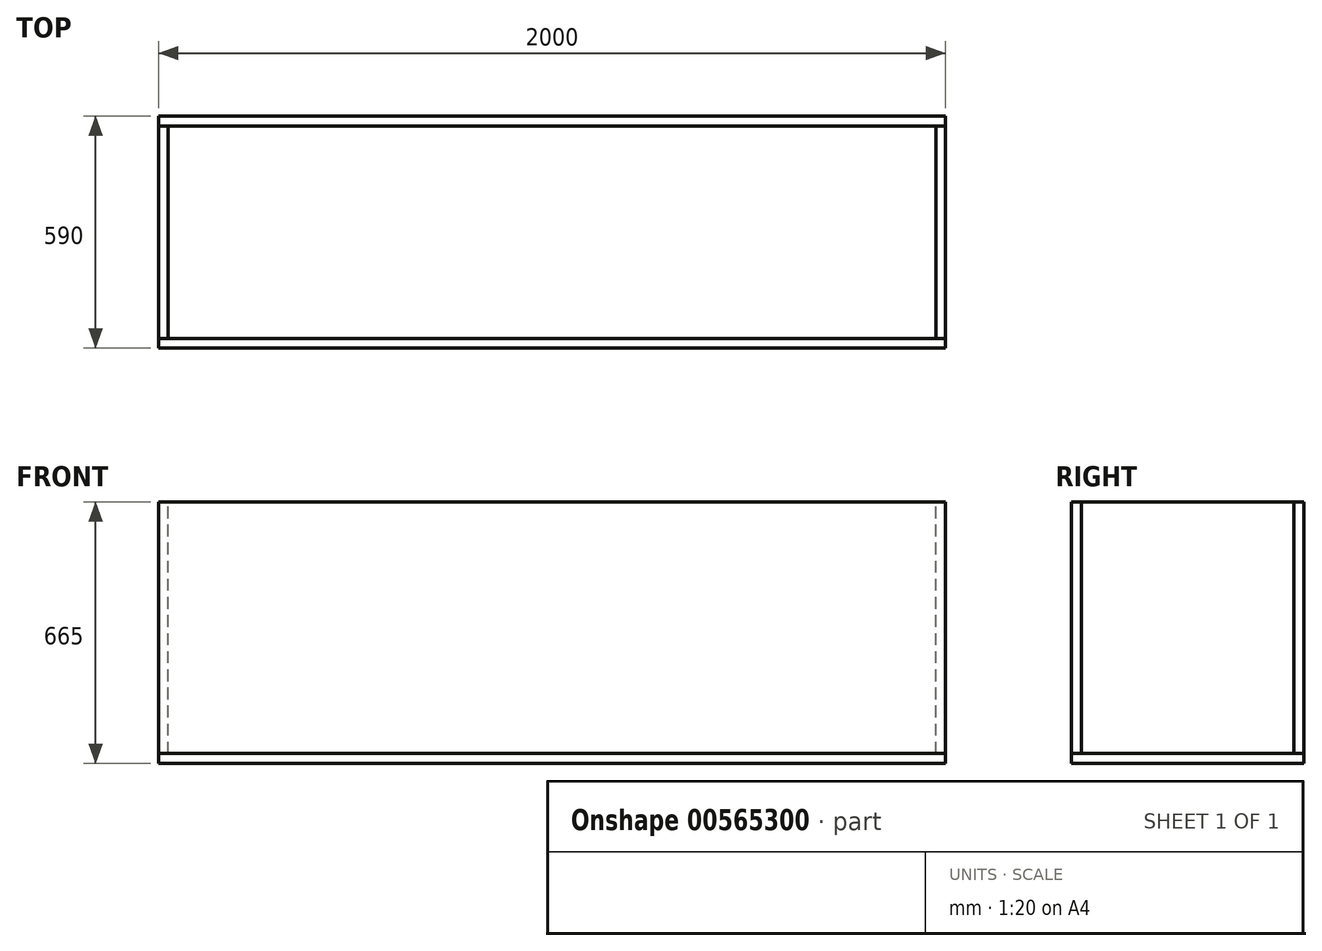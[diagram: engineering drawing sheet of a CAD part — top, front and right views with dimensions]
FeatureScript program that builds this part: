
annotation { "Feature Type Name" : "Feature", "Feature Type Description" : "" }
export const myFeature = defineFeature(function(context is Context, id is Id, definition is map)
    precondition{}
    {
        {
            var Q0;
            Q0=qCreatedBy(makeId("Front.planeOp"),FACE);
            var sketch = newSketch(context, id + "F0", { "sketchPlane" : qUnion([Q0])});
            skLineSegment(sketch, "E0.bottom", {"start": v(0, 0) * mm, "end": v(2000, 0) * mm});
            skLineSegment(sketch, "E0.top", {"start": v(0, 640) * mm, "end": v(2000, 640) * mm});
            skLineSegment(sketch, "E0.left", {"start": v(0, 0) * mm, "end": v(0, 640) * mm});
            skLineSegment(sketch, "E0.right", {"start": v(2000, 0) * mm, "end": v(2000, 640) * mm});
            skSolve(sketch);
        }
        {
            var Q0;
            Q0 = qSketchRegion(id + "F0", true);
            extrude(context, id + "F1", {"entities" : qUnion([Q0]), "depth" : 25 * mm, "offsetDistance" : 25 * mm});
        }
        {
            var Q0;
            Q0=qCreatedBy(makeId("Top.planeOp"),FACE);
            var sketch = newSketch(context, id + "F2", { "sketchPlane" : qUnion([Q0])});
            skLineSegment(sketch, "E1.bottom", {"start": v(0, 0) * mm, "end": v(2000, 0) * mm});
            skLineSegment(sketch, "E1.top", {"start": v(0, -590) * mm, "end": v(2000, -590) * mm});
            skLineSegment(sketch, "E1.left", {"start": v(0, 0) * mm, "end": v(0, -590) * mm});
            skLineSegment(sketch, "E1.right", {"start": v(2000, 0) * mm, "end": v(2000, -590) * mm});
            skSolve(sketch);
        }
        {
            var Q0;
            Q0=makeQuery(id+"F2.imprint","IMPRINT",FACE,{"disambiguationData":[TD([[makeQuery(id+"F2.imprint","IMPRINT",EDGE,{"derivedFrom":sQuery(id+"F2.wireOp",EDGE,"E1.bottom")}),-1.0]])]});
            extrude(context, id + "F3", {"entities" : qUnion([Q0]), "oppositeDirection" : true, "depth" : 25 * mm, "offsetDistance" : 25 * mm});
        }
        {
            var Q0;
            Q0=makeQuery(id+"F1.opExtrude","SWEPT_BODY",BODY,{"disambiguationData":[OSD([sQuery(id+"F0.wireOp",EDGE,"E0.bottom"),sQuery(id+"F0.wireOp",EDGE,"E0.top"),sQuery(id+"F0.wireOp",EDGE,"E0.left"),sQuery(id+"F0.wireOp",EDGE,"E0.right")])]});
            var Q1;
            Q1=makeQuery(id+"F3.opExtrude","SWEPT_FACE",FACE,{"disambiguationData":[OSD([sQuery(id+"F2.wireOp",EDGE,"E1.top")])]});
            var Q2;
            Q2=makeQuery(id+"F3.opExtrude","CAP_EDGE",EDGE,{"disambiguationData":[OSD([sQuery(id+"F2.wireOp",EDGE,"E1.left")])],"isStart":true});
            transform(context, id + "F4", {"entities" : qUnion([Q0]), "transformType" : TransformType.TRANSLATION_DISTANCE, "transformDirection" : qUnion([Q1, Q2]), "distance" : 565 * mm, "makeCopy" : true});
        }
        {
            var Q0;
            Q0=qCreatedBy(makeId("Right.planeOp"),FACE);
            var sketch = newSketch(context, id + "F5", { "sketchPlane" : qUnion([Q0])});
            skLineSegment(sketch, "E2.bottom", {"start": v(-25, 0) * mm, "end": v(-565, 0) * mm});
            skLineSegment(sketch, "E2.top", {"start": v(-25, 640) * mm, "end": v(-565, 640) * mm});
            skLineSegment(sketch, "E2.left", {"start": v(-25, 0) * mm, "end": v(-25, 640) * mm});
            skLineSegment(sketch, "E2.right", {"start": v(-565, 0) * mm, "end": v(-565, 640) * mm});
            skSolve(sketch);
        }
        {
            var Q0;
            Q0 = qSketchRegion(id + "F5", true);
            extrude(context, id + "F6", {"entities" : qUnion([Q0]), "depth" : 25 * mm, "offsetDistance" : 25 * mm});
        }
        {
            var Q0;
            Q0=makeQuery(id+"F3.opExtrude","SWEPT_FACE",FACE,{"disambiguationData":[OSD([sQuery(id+"F2.wireOp",EDGE,"E1.right")])]});
            var sketch = newSketch(context, id + "F7", { "sketchPlane" : qUnion([Q0])});
            skLineSegment(sketch, "E3.bottom", {"start": v(-565, 0) * mm, "end": v(-25, 0) * mm});
            skLineSegment(sketch, "E3.top", {"start": v(-565, 640) * mm, "end": v(-25, 640) * mm});
            skLineSegment(sketch, "E3.left", {"start": v(-565, 0) * mm, "end": v(-565, 640) * mm});
            skLineSegment(sketch, "E3.right", {"start": v(-25, 0) * mm, "end": v(-25, 640) * mm});
            skSolve(sketch);
        }
        {
            var Q0;
            Q0 = qSketchRegion(id + "F7", true);
            extrude(context, id + "F8", {"entities" : qUnion([Q0]), "oppositeDirection" : true, "depth" : 25 * mm, "offsetDistance" : 25 * mm});
        }
    });
